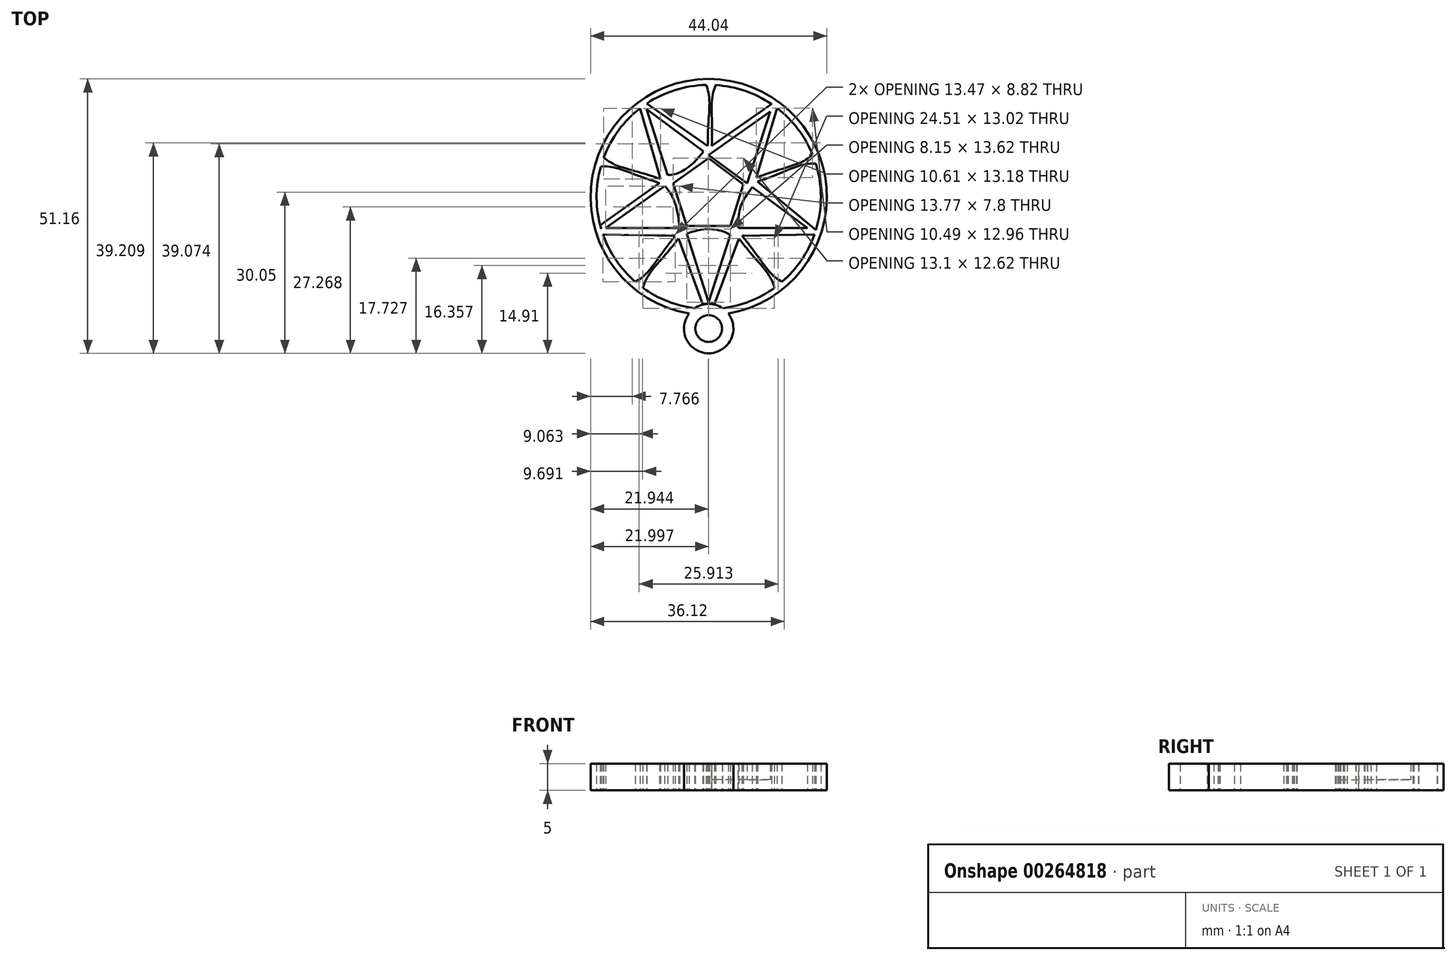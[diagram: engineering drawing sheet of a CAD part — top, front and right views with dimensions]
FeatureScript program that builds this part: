
annotation { "Feature Type Name" : "Feature", "Feature Type Description" : "" }
export const myFeature = defineFeature(function(context is Context, id is Id, definition is map)
    precondition{}
    {
        {
            var Q0;
            Q0=qCreatedBy(makeId("Top.planeOp"),FACE);
            var sketch = newSketch(context, id + "F0", { "sketchPlane" : qUnion([Q0])});
            skCircle(sketch, "E0", {"center": v(0, 0) * mm, "radius": 22.02 * mm});
            skLineSegment(sketch, "E1", {"start": v(0, 0) * mm, "end": v(0, 22.02) * mm, "construction": true});
            skLineSegment(sketch, "E2", {"start": v(0, 0) * mm, "end": v(20.72, 7.45) * mm, "construction": true});
            skLineSegment(sketch, "E3", {"start": v(0, 0) * mm, "end": v(13.06, -17.72) * mm, "construction": true});
            skLineSegment(sketch, "E4", {"start": v(0, 0) * mm, "end": v(-13.06, -17.72) * mm, "construction": true});
            skLineSegment(sketch, "E5", {"start": v(0, 0) * mm, "end": v(-20.91, 6.88) * mm, "construction": true});
            skLineSegment(sketch, "E6", {"start": v(-13.06, 17.72) * mm, "end": v(0, -22.02) * mm, "construction": true});
            skLineSegment(sketch, "E7", {"start": v(0, -22.02) * mm, "end": v(13.06, 17.72) * mm, "construction": true});
            skLineSegment(sketch, "E8", {"start": v(13.06, 17.72) * mm, "end": v(-20.91, -6.88) * mm, "construction": true});
            skLineSegment(sketch, "E9", {"start": v(-20.91, -6.88) * mm, "end": v(20.72, -6.88) * mm, "construction": true});
            skLineSegment(sketch, "E10", {"start": v(20.72, -6.88) * mm, "end": v(-13.06, 17.72) * mm, "construction": true});
            skCircle(sketch, "E11", {"center": v(0, 0) * mm, "radius": 20.9 * mm});
            skLineSegment(sketch, "E12", {"start": v(-11.47, 15.95) * mm, "end": v(0, -18.94) * mm});
            skLineSegment(sketch, "E13", {"start": v(0, -18.94) * mm, "end": v(11.36, 15.61) * mm});
            skLineSegment(sketch, "E14", {"start": v(11.36, 15.61) * mm, "end": v(-18.96, -5.83) * mm});
            skLineSegment(sketch, "E15", {"start": v(-18.96, -5.83) * mm, "end": v(18.12, -5.83) * mm});
            skLineSegment(sketch, "E16", {"start": v(18.12, -5.83) * mm, "end": v(-11.47, 15.95) * mm});
            skSolve(sketch);
        }
        {
            var Q0;
            Q0=makeQuery(id+"F0.imprint","IMPRINT",FACE,{"disambiguationData":[TD([[makeQuery(id+"F0.imprint","IMPRINT",EDGE,{"derivedFrom":sQuery(id+"F0.wireOp",EDGE,"E11")}),1.0]])]});
            var Q1;
            {var subQ0=sQuery(id+"F0.wireOp",EDGE,"E14");var subQ1=sQuery(id+"F0.wireOp",EDGE,"E13");var subQ2=makeQuery(id+"F0.imprint","INTERSECT",VERTEX,{"derivedFrom":[subQ1,subQ0]});Q1=makeQuery(id+"F0.imprint","IMPRINT",FACE,{"disambiguationData":[TD([[makeQuery(id+"F0.imprint","IMPRINT",EDGE,{"disambiguationData":[TD([[subQ2,1.0]])],"derivedFrom":subQ1}),1.0]])]});}
            var Q2;
            {var subQ0=sQuery(id+"F0.wireOp",EDGE,"E16");var subQ1=sQuery(id+"F0.wireOp",EDGE,"E12");var subQ2=makeQuery(id+"F0.imprint","INTERSECT",VERTEX,{"derivedFrom":[subQ1,subQ0]});Q2=makeQuery(id+"F0.imprint","IMPRINT",FACE,{"disambiguationData":[TD([[makeQuery(id+"F0.imprint","IMPRINT",EDGE,{"disambiguationData":[TD([[subQ2,-1.0]])],"derivedFrom":subQ1}),1.0]])]});}
            var Q3;
            {var subQ0=sQuery(id+"F0.wireOp",EDGE,"E14");var subQ1=sQuery(id+"F0.wireOp",EDGE,"E12");var subQ2=makeQuery(id+"F0.imprint","INTERSECT",VERTEX,{"derivedFrom":[subQ1,subQ0]});Q3=makeQuery(id+"F0.imprint","IMPRINT",FACE,{"disambiguationData":[TD([[makeQuery(id+"F0.imprint","IMPRINT",EDGE,{"disambiguationData":[TD([[subQ2,-1.0]])],"derivedFrom":subQ1}),-1.0]])]});}
            var Q4;
            {var subQ0=sQuery(id+"F0.wireOp",EDGE,"E13");var subQ1=sQuery(id+"F0.wireOp",EDGE,"E12");var subQ2=makeQuery(id+"F0.imprint","INTERSECT",VERTEX,{"derivedFrom":[subQ1,subQ0]});Q4=makeQuery(id+"F0.imprint","IMPRINT",FACE,{"disambiguationData":[TD([[makeQuery(id+"F0.imprint","IMPRINT",EDGE,{"disambiguationData":[TD([[subQ2,1.0]])],"derivedFrom":subQ1}),1.0]])]});}
            var Q5;
            {var subQ0=sQuery(id+"F0.wireOp",EDGE,"E15");var subQ1=sQuery(id+"F0.wireOp",EDGE,"E13");var subQ2=makeQuery(id+"F0.imprint","INTERSECT",VERTEX,{"derivedFrom":[subQ1,subQ0]});Q5=makeQuery(id+"F0.imprint","IMPRINT",FACE,{"disambiguationData":[TD([[makeQuery(id+"F0.imprint","IMPRINT",EDGE,{"disambiguationData":[TD([[subQ2,-1.0]])],"derivedFrom":subQ1}),-1.0]])]});}
            var Q6;
            {var subQ1=sQuery(id+"F0.wireOp",EDGE,"E12");var subQ5=sQuery(id+"F0.wireOp",EDGE,"E14");var subQ6=makeQuery(id+"F0.imprint","INTERSECT",VERTEX,{"derivedFrom":[subQ1,subQ5]});Q6=makeQuery(id+"F0.imprint","IMPRINT",FACE,{"disambiguationData":[TD([[makeQuery(id+"F0.imprint","IMPRINT",EDGE,{"disambiguationData":[TD([[subQ6,-1.0]])],"derivedFrom":subQ1}),1.0]])]});}
            extrude(context, id + "F1", {"entities" : qUnion([Q0, Q1, Q2, Q3, Q4, Q5, Q6]), "depth" : 2 * mm, "offsetDistance" : 25 * mm});
        }
        {
            var Q0;
            Q0=makeQuery(id+"F0.imprint","IMPRINT",FACE,{"disambiguationData":[TD([[makeQuery(id+"F0.imprint","IMPRINT",EDGE,{"derivedFrom":sQuery(id+"F0.wireOp",EDGE,"E0")}),1.0]])]});
            extrude(context, id + "F2", {"entities" : qUnion([Q0]), "operationType" : NewBodyOperationType.ADD, "depth" : 5 * mm, "offsetDistance" : 25 * mm});
        }
        {
            var Q0;
            Q0=makeQuery(id+"F1.opExtrude","CAP_FACE",FACE,{"disambiguationData":[OSD([sQuery(id+"F0.wireOp",EDGE,"E11")])],"isStart":false});
            var sketch = newSketch(context, id + "F3", { "sketchPlane" : qUnion([Q0])});
            skLineSegment(sketch, "E17", {"start": v(-11.59, 16.36) * mm, "end": v(0, -19.6) * mm});
            skLineSegment(sketch, "E18", {"start": v(0, -19.6) * mm, "end": v(11.46, 15.95) * mm});
            skLineSegment(sketch, "E19", {"start": v(11.46, 15.95) * mm, "end": v(-19.22, -5.77) * mm});
            skLineSegment(sketch, "E20", {"start": v(-19.22, -5.77) * mm, "end": v(18.4, -5.77) * mm});
            skLineSegment(sketch, "E21", {"start": v(18.4, -5.77) * mm, "end": v(-11.59, 16.36) * mm});
            skPoint(sketch, "E22.2.internal.snap0", {"position": v(-3.88, 5.1) * mm});
            skFitSpline(sketch, "E22", {"points": [v(-7.63, 4.09) * mm, v(-6, 4.35) * mm, v(-3.88, 5.51) * mm, v(-1.86, 7.4) * mm, v(-0.97, 8.52) * mm], "startDerivative": vector(7.1, 0.61) * mm, "endDerivative": vector(3.7, 5) * mm});
            skFitSpline(sketch, "E23.MirrorCS", {"points": [v(7.63, 4.09) * mm, v(6, 4.35) * mm, v(3.88, 5.51) * mm, v(1.86, 7.4) * mm, v(0.97, 8.52) * mm], "startDerivative": vector(-7.1, 0.61) * mm, "endDerivative": vector(-3.7, 5) * mm});
            skFitSpline(sketch, "E24", {"points": [v(0.97, 8.52) * mm, v(1.86, 7.4) * mm, v(3.88, 5.51) * mm, v(6, 4.35) * mm, v(7.63, 4.09) * mm], "startDerivative": vector(3.71, -5.02) * mm, "endDerivative": vector(7.1, -0.61) * mm});
            skFitSpline(sketch, "E25", {"points": [v(-8.2, 2.03) * mm, v(-7.19, 0.78) * mm, v(-6.13, -1.62) * mm, v(-5.57, -4.53) * mm, v(-5.44, -5.77) * mm], "startDerivative": vector(4.84, -5) * mm, "endDerivative": vector(0.3, -5.7) * mm});
            skPoint(sketch, "E26", {"position": v(-5.8, -1.62) * mm});
            skFitSpline(sketch, "E27", {"points": [v(-4.1, -6.89) * mm, v(-2.2, -6.27) * mm, v(0, -5.98) * mm, v(2.75, -6.44) * mm, v(4.05, -7.03) * mm], "startDerivative": vector(7.54, 3.7) * mm, "endDerivative": vector(5.89, -2.67) * mm});
            skFitSpline(sketch, "E28", {"points": [v(8.1, 1.83) * mm, v(6.5, -0.54) * mm, v(5.83, -2.25) * mm, v(5.5, -4.78) * mm, v(5.54, -5.77) * mm], "startDerivative": vector(-5.96, -8.34) * mm, "endDerivative": vector(0.52, -4.8) * mm});
            skFitSpline(sketch, "E29", {"points": [v(-20.36, 5.66) * mm, v(-17.82, 5.55) * mm, v(-12.86, 3.85) * mm, v(-9.19, 2.62) * mm], "startDerivative": vector(8.48, 0.55) * mm, "endDerivative": vector(10.23, -3.2) * mm});
            skFitSpline(sketch, "E30.MirrorCS", {"points": [v(-19.75, 7.53) * mm, v(-17.64, 6.1) * mm, v(-12.63, 4.53) * mm, v(-8.95, 3.34) * mm], "startDerivative": vector(6.5, -5.47) * mm, "endDerivative": vector(10.13, -3.49) * mm});
            skLineSegment(sketch, "E31", {"start": v(-19.22, -5.77) * mm, "end": v(0, 0) * mm, "construction": true});
            skLineSegment(sketch, "E32", {"start": v(0, 0) * mm, "end": v(11.46, 15.95) * mm, "construction": true});
            skLineSegment(sketch, "E33", {"start": v(-11.59, 16.36) * mm, "end": v(-10.84, 15.8) * mm, "construction": true});
            skLineSegment(sketch, "E34", {"start": v(-11.59, 16.36) * mm, "end": v(0, 0) * mm, "construction": true});
            skLineSegment(sketch, "E35", {"start": v(0, -0.7) * mm, "end": v(0, 0) * mm, "construction": true});
            skFitSpline(sketch, "E36.MirrorCS", {"points": [v(-13.87, -15.94) * mm, v(-11.8, -14.46) * mm, v(-8.6, -10.3) * mm, v(-6.22, -7.25) * mm], "startDerivative": vector(7.38, 4.21) * mm, "endDerivative": vector(6.77, 8.3) * mm});
            skFitSpline(sketch, "E37.MirrorCS", {"points": [v(-12.33, -17.17) * mm, v(-11.35, -14.82) * mm, v(-8.05, -10.74) * mm, v(-5.62, -7.72) * mm], "startDerivative": vector(2.4, 8.15) * mm, "endDerivative": vector(6.53, 8.5) * mm});
            skFitSpline(sketch, "E38.MirrorCS", {"points": [v(1.41, 21.09) * mm, v(0.67, 18.65) * mm, v(0.63, 13.4) * mm, v(0.57, 9.54) * mm], "startDerivative": vector(-3.33, -7.82) * mm, "endDerivative": vector(-0.37, -10.7) * mm});
            skFitSpline(sketch, "E39.MirrorCS", {"points": [v(-0.56, 21.13) * mm, v(0.09, 18.67) * mm, v(-0.08, 13.42) * mm, v(-0.19, 9.55) * mm], "startDerivative": vector(3, -7.94) * mm, "endDerivative": vector(-0.07, -10.72) * mm});
            skFitSpline(sketch, "E40.MirrorCS", {"points": [v(19.53, 8.08) * mm, v(17.46, 6.6) * mm, v(12.5, 4.88) * mm, v(8.85, 3.59) * mm], "startDerivative": vector(-6.34, -5.65) * mm, "endDerivative": vector(-10.03, -3.77) * mm});
            skFitSpline(sketch, "E41.MirrorCS", {"points": [v(20.2, 6.22) * mm, v(17.66, 6.05) * mm, v(12.74, 4.2) * mm, v(9.1, 2.87) * mm], "startDerivative": vector(-8.49, 0.31) * mm, "endDerivative": vector(-10.13, -3.49) * mm});
            skFitSpline(sketch, "E42.MirrorCS", {"points": [v(12.33, -17.17) * mm, v(11.35, -14.82) * mm, v(8.05, -10.74) * mm, v(5.62, -7.72) * mm], "startDerivative": vector(-2.4, 8.15) * mm, "endDerivative": vector(-6.53, 8.5) * mm});
            skFitSpline(sketch, "E43.MirrorCS", {"points": [v(13.87, -15.94) * mm, v(11.8, -14.46) * mm, v(8.6, -10.3) * mm, v(6.22, -7.25) * mm], "startDerivative": vector(-7.38, 4.21) * mm, "endDerivative": vector(-6.77, 8.3) * mm});
            skLineSegment(sketch, "E44", {"start": v(0, 0) * mm, "end": v(18.4, -5.77) * mm, "construction": true});
            skLineSegment(sketch, "E45", {"start": v(-19.76, -7) * mm, "end": v(-6.22, -7.25) * mm});
            skLineSegment(sketch, "E46", {"start": v(-19.76, -7) * mm, "end": v(-20.22, -5.27) * mm});
            skLineSegment(sketch, "E47", {"start": v(-20.22, -5.27) * mm, "end": v(-9.19, 2.62) * mm});
            skLineSegment(sketch, "E48", {"start": v(-19.75, 7.53) * mm, "end": v(-20.36, 5.66) * mm});
            skLineSegment(sketch, "E49", {"start": v(-13.87, -15.94) * mm, "end": v(-12.33, -17.17) * mm});
            skLineSegment(sketch, "E50", {"start": v(-5.62, -7.72) * mm, "end": v(-0.76, -20.96) * mm});
            skLineSegment(sketch, "E51", {"start": v(-0.76, -20.96) * mm, "end": v(0.71, -20.99) * mm});
            skLineSegment(sketch, "E52", {"start": v(0.71, -20.99) * mm, "end": v(5.62, -7.72) * mm});
            skLineSegment(sketch, "E53", {"start": v(12.33, -17.17) * mm, "end": v(13.87, -15.94) * mm});
            skLineSegment(sketch, "E54", {"start": v(6.22, -7.25) * mm, "end": v(19.85, -7) * mm});
            skLineSegment(sketch, "E55", {"start": v(19.85, -7) * mm, "end": v(20.08, -6.26) * mm});
            skLineSegment(sketch, "E56", {"start": v(9.1, 2.87) * mm, "end": v(20.08, -6.26) * mm});
            skLineSegment(sketch, "E57", {"start": v(19.53, 8.08) * mm, "end": v(20.2, 6.22) * mm});
            skLineSegment(sketch, "E58", {"start": v(8.85, 3.59) * mm, "end": v(12.8, 16.66) * mm});
            skLineSegment(sketch, "E59", {"start": v(12.8, 16.66) * mm, "end": v(11.8, 17.4) * mm});
            skLineSegment(sketch, "E60", {"start": v(11.8, 17.4) * mm, "end": v(0.57, 9.54) * mm});
            skLineSegment(sketch, "E61", {"start": v(1.41, 21.09) * mm, "end": v(-0.56, 21.13) * mm});
            skLineSegment(sketch, "E62", {"start": v(-0.19, 9.55) * mm, "end": v(-11.66, 17.51) * mm});
            skLineSegment(sketch, "E63", {"start": v(-11.66, 17.51) * mm, "end": v(-12.84, 16.68) * mm});
            skLineSegment(sketch, "E64", {"start": v(-12.84, 16.68) * mm, "end": v(-8.95, 3.34) * mm});
            skLineSegment(sketch, "E65", {"start": v(-6.63, 2.52) * mm, "end": v(-4.07, -5.4) * mm});
            skLineSegment(sketch, "E66", {"start": v(-4.07, -5.4) * mm, "end": v(4.07, -5.4) * mm});
            skLineSegment(sketch, "E67", {"start": v(4.07, -5.4) * mm, "end": v(6.47, 2.38) * mm});
            skLineSegment(sketch, "E68", {"start": v(6.47, 2.38) * mm, "end": v(0, 7.22) * mm});
            skLineSegment(sketch, "E69", {"start": v(0, 7.22) * mm, "end": v(-6.63, 2.52) * mm});
            skCircle(sketch, "E70", {"center": v(0, -24.64) * mm, "radius": 4.75 * mm});
            skCircle(sketch, "E71", {"center": v(0, -24.64) * mm, "radius": 2.5 * mm});
            skLineSegment(sketch, "E72", {"start": v(2.5, -24.53) * mm, "end": v(-2.5, -24.64) * mm, "construction": true});
            skSolve(sketch);
        }
        {
            var Q0;
            {var subQ3=sQuery(id+"F3.wireOp",EDGE,"E22");Q0=makeQuery(id+"F3.imprint","IMPRINT",FACE,{"disambiguationData":[TD([[makeQuery(id+"F3.imprint","IMPRINT",EDGE,{"derivedFrom":subQ3}),1.0]])]});}
            var Q1;
            {var subQ3=sQuery(id+"F3.wireOp",EDGE,"E24");var subQ6=makeQuery(id+"F3.imprint","IMPRINT",VERTEX,{"derivedFrom":subQ3});Q1=makeQuery(id+"F3.imprint","IMPRINT",FACE,{"disambiguationData":[TD([[makeQuery(id+"F3.imprint","IMPRINT",EDGE,{"disambiguationData":[TD([[subQ6,1.0]])],"derivedFrom":subQ3}),1.0]])]});}
            var Q2;
            {var subQ3=sQuery(id+"F3.wireOp",EDGE,"E25");Q2=makeQuery(id+"F3.imprint","IMPRINT",FACE,{"disambiguationData":[TD([[makeQuery(id+"F3.imprint","IMPRINT",EDGE,{"derivedFrom":subQ3}),-1.0]])]});}
            var Q3;
            {var subQ3=sQuery(id+"F3.wireOp",EDGE,"E27");Q3=makeQuery(id+"F3.imprint","IMPRINT",FACE,{"disambiguationData":[TD([[makeQuery(id+"F3.imprint","IMPRINT",EDGE,{"derivedFrom":subQ3}),-1.0]])]});}
            var Q4;
            {var subQ3=sQuery(id+"F3.wireOp",EDGE,"E28");Q4=makeQuery(id+"F3.imprint","IMPRINT",FACE,{"disambiguationData":[TD([[makeQuery(id+"F3.imprint","IMPRINT",EDGE,{"derivedFrom":subQ3}),1.0]])]});}
            var Q5;
            Q5=makeQuery(id+"F3.imprint","IMPRINT",FACE,{"disambiguationData":[TD([[makeQuery(id+"F3.imprint","IMPRINT",EDGE,{"derivedFrom":sQuery(id+"F3.wireOp",EDGE,"E65")}),1.0]])]});
            extrude(context, id + "F4", {"entities" : qUnion([Q0, Q1, Q2, Q3, Q4, Q5]), "operationType" : NewBodyOperationType.ADD, "depth" : 2 * mm, "offsetDistance" : 25 * mm});
        }
        {
            var Q0;
            Q0=makeQuery(id+"F3.imprint","IMPRINT",FACE,{"disambiguationData":[TD([[makeQuery(id+"F3.imprint","IMPRINT",EDGE,{"derivedFrom":sQuery(id+"F3.wireOp",EDGE,"E29")}),1.0]])]});
            var Q1;
            {var subQ5=sQuery(id+"F3.wireOp",EDGE,"E25");Q1=makeQuery(id+"F3.imprint","IMPRINT",FACE,{"disambiguationData":[TD([[makeQuery(id+"F3.imprint","IMPRINT",EDGE,{"derivedFrom":subQ5}),1.0]])]});}
            var Q2;
            {var subQ0=sQuery(id+"F3.wireOp",EDGE,"E22");Q2=makeQuery(id+"F3.imprint","IMPRINT",FACE,{"disambiguationData":[TD([[makeQuery(id+"F3.imprint","IMPRINT",EDGE,{"derivedFrom":subQ0}),-1.0]])]});}
            var Q3;
            {var subQ5=sQuery(id+"F3.wireOp",EDGE,"E24");var subQ7=makeQuery(id+"F3.imprint","IMPRINT",VERTEX,{"derivedFrom":subQ5});Q3=makeQuery(id+"F3.imprint","IMPRINT",FACE,{"disambiguationData":[TD([[makeQuery(id+"F3.imprint","IMPRINT",EDGE,{"disambiguationData":[TD([[subQ7,1.0]])],"derivedFrom":subQ5}),-1.0]])]});}
            var Q4;
            {var subQ5=sQuery(id+"F3.wireOp",EDGE,"E28");Q4=makeQuery(id+"F3.imprint","IMPRINT",FACE,{"disambiguationData":[TD([[makeQuery(id+"F3.imprint","IMPRINT",EDGE,{"derivedFrom":subQ5}),-1.0]])]});}
            var Q5;
            Q5=makeQuery(id+"F3.imprint","IMPRINT",FACE,{"disambiguationData":[TD([[makeQuery(id+"F3.imprint","IMPRINT",EDGE,{"derivedFrom":sQuery(id+"F3.wireOp",EDGE,"E65")}),-1.0]])]});
            var Q6;
            {var subQ0=sQuery(id+"F3.wireOp",EDGE,"E27");Q6=makeQuery(id+"F3.imprint","IMPRINT",FACE,{"disambiguationData":[TD([[makeQuery(id+"F3.imprint","IMPRINT",EDGE,{"derivedFrom":subQ0}),1.0]])]});}
            var Q7;
            {var subQ33=sQuery(id+"F3.wireOp",EDGE,"E47");Q7=makeQuery(id+"F3.imprint","IMPRINT",FACE,{"disambiguationData":[TD([[makeQuery(id+"F3.imprint","IMPRINT",EDGE,{"derivedFrom":subQ33}),-1.0]])]});}
            extrude(context, id + "F5", {"entities" : qUnion([Q0, Q1, Q2, Q3, Q4, Q5, Q6, Q7]), "operationType" : NewBodyOperationType.ADD, "depth" : 3 * mm, "offsetDistance" : 25 * mm});
        }
        {
            var Q0;
            Q0=qCreatedBy(makeId("Top.planeOp"),FACE);
            var sketch = newSketch(context, id + "F6", { "sketchPlane" : qUnion([Q0])});
            skCircle(sketch, "E73", {"center": v(0, -24.54) * mm, "radius": 4.6 * mm});
            skCircle(sketch, "E74", {"center": v(0, -24.54) * mm, "radius": 2.49 * mm});
            skSolve(sketch);
        }
        {
            var Q0;
            Q0=makeQuery(id+"F6.imprint","IMPRINT",FACE,{"disambiguationData":[TD([[makeQuery(id+"F6.imprint","IMPRINT",EDGE,{"derivedFrom":sQuery(id+"F6.wireOp",EDGE,"E73")}),1.0]])]});
            extrude(context, id + "F7", {"entities" : qUnion([Q0]), "operationType" : NewBodyOperationType.ADD, "depth" : 5 * mm, "offsetDistance" : 25 * mm});
        }
        {
            var Q0;
            {var subQ0=sQuery(id+"F0.wireOp",EDGE,"E11");Q0=makeQuery(id+"F5.boolean.opBoolean","SPLIT",FACE,{"disambiguationData":[TD([makeQuery(id+"F5.opExtrude","SWEPT_FACE",FACE,{"disambiguationData":[OSD([sQuery(id+"F3.wireOp",EDGE,"E39.MirrorCS")])]})])],"derivedFrom":makeQuery(id+"F1.opExtrude","CAP_FACE",FACE,{"disambiguationData":[OSD([subQ0])],"isStart":false})});}
            var Q1;
            Q1=makeQuery(id+"F4.opExtrude","CAP_FACE",FACE,{"disambiguationData":[OSD([sQuery(id+"F3.wireOp",EDGE,"E17"),sQuery(id+"F3.wireOp",EDGE,"E21"),sQuery(id+"F3.wireOp",EDGE,"E22")])],"isStart":false});
            var Q2;
            {var subQ0=sQuery(id+"F0.wireOp",EDGE,"E11");Q2=makeQuery(id+"F5.boolean.opBoolean","SPLIT",FACE,{"disambiguationData":[TD([makeQuery(id+"F5.opExtrude","SWEPT_FACE",FACE,{"disambiguationData":[OSD([sQuery(id+"F3.wireOp",EDGE,"E30.MirrorCS")])]})])],"derivedFrom":makeQuery(id+"F1.opExtrude","CAP_FACE",FACE,{"disambiguationData":[OSD([subQ0])],"isStart":false})});}
            var Q3;
            {var subQ0=sQuery(id+"F0.wireOp",EDGE,"E11");Q3=makeQuery(id+"F5.boolean.opBoolean","SPLIT",FACE,{"disambiguationData":[TD([makeQuery(id+"F5.opExtrude","SWEPT_FACE",FACE,{"disambiguationData":[OSD([sQuery(id+"F3.wireOp",EDGE,"E29")])]})])],"derivedFrom":makeQuery(id+"F1.opExtrude","CAP_FACE",FACE,{"disambiguationData":[OSD([subQ0])],"isStart":false})});}
            var Q4;
            Q4=makeQuery(id+"F4.opExtrude","CAP_FACE",FACE,{"disambiguationData":[OSD([sQuery(id+"F3.wireOp",EDGE,"E19"),sQuery(id+"F3.wireOp",EDGE,"E20"),sQuery(id+"F3.wireOp",EDGE,"E25")])],"isStart":false});
            var Q5;
            {var subQ0=sQuery(id+"F0.wireOp",EDGE,"E11");Q5=makeQuery(id+"F5.boolean.opBoolean","SPLIT",FACE,{"disambiguationData":[TD([makeQuery(id+"F5.opExtrude","SWEPT_FACE",FACE,{"disambiguationData":[OSD([sQuery(id+"F3.wireOp",EDGE,"E36.MirrorCS")])]})])],"derivedFrom":makeQuery(id+"F1.opExtrude","CAP_FACE",FACE,{"disambiguationData":[OSD([subQ0])],"isStart":false})});}
            var Q6;
            {var subQ0=sQuery(id+"F0.wireOp",EDGE,"E11");Q6=makeQuery(id+"F5.boolean.opBoolean","SPLIT",FACE,{"disambiguationData":[TD([makeQuery(id+"F5.opExtrude","SWEPT_FACE",FACE,{"disambiguationData":[OSD([sQuery(id+"F3.wireOp",EDGE,"E37.MirrorCS")])]})])],"derivedFrom":makeQuery(id+"F1.opExtrude","CAP_FACE",FACE,{"disambiguationData":[OSD([subQ0])],"isStart":false})});}
            var Q7;
            Q7=makeQuery(id+"F4.opExtrude","CAP_FACE",FACE,{"disambiguationData":[OSD([sQuery(id+"F3.wireOp",EDGE,"E17"),sQuery(id+"F3.wireOp",EDGE,"E18"),sQuery(id+"F3.wireOp",EDGE,"E27")])],"isStart":false});
            var Q8;
            Q8=makeQuery(id+"F4.opExtrude","CAP_FACE",FACE,{"disambiguationData":[OSD([sQuery(id+"F3.wireOp",EDGE,"E65"),sQuery(id+"F3.wireOp",EDGE,"E66"),sQuery(id+"F3.wireOp",EDGE,"E67"),sQuery(id+"F3.wireOp",EDGE,"E68"),sQuery(id+"F3.wireOp",EDGE,"E69")])],"isStart":false});
            var Q9;
            {var subQ0=sQuery(id+"F0.wireOp",EDGE,"E11");Q9=makeQuery(id+"F5.boolean.opBoolean","SPLIT",FACE,{"disambiguationData":[TD([makeQuery(id+"F5.opExtrude","SWEPT_FACE",FACE,{"disambiguationData":[OSD([sQuery(id+"F3.wireOp",EDGE,"E43.MirrorCS")])]})])],"derivedFrom":makeQuery(id+"F1.opExtrude","CAP_FACE",FACE,{"disambiguationData":[OSD([subQ0])],"isStart":false})});}
            var Q10;
            Q10=makeQuery(id+"F4.opExtrude","CAP_FACE",FACE,{"disambiguationData":[OSD([sQuery(id+"F3.wireOp",EDGE,"E20"),sQuery(id+"F3.wireOp",EDGE,"E21"),sQuery(id+"F3.wireOp",EDGE,"E28")])],"isStart":false});
            var Q11;
            {var subQ0=sQuery(id+"F0.wireOp",EDGE,"E11");Q11=makeQuery(id+"F5.boolean.opBoolean","SPLIT",FACE,{"disambiguationData":[TD([makeQuery(id+"F5.opExtrude","SWEPT_FACE",FACE,{"disambiguationData":[OSD([sQuery(id+"F3.wireOp",EDGE,"E41.MirrorCS")])]})])],"derivedFrom":makeQuery(id+"F1.opExtrude","CAP_FACE",FACE,{"disambiguationData":[OSD([subQ0])],"isStart":false})});}
            var Q12;
            {var subQ0=sQuery(id+"F0.wireOp",EDGE,"E11");Q12=makeQuery(id+"F5.boolean.opBoolean","SPLIT",FACE,{"disambiguationData":[TD([makeQuery(id+"F5.opExtrude","SWEPT_FACE",FACE,{"disambiguationData":[OSD([sQuery(id+"F3.wireOp",EDGE,"E40.MirrorCS")])]})])],"derivedFrom":makeQuery(id+"F1.opExtrude","CAP_FACE",FACE,{"disambiguationData":[OSD([subQ0])],"isStart":false})});}
            var Q13;
            Q13=makeQuery(id+"F4.opExtrude","CAP_FACE",FACE,{"disambiguationData":[OSD([sQuery(id+"F3.wireOp",EDGE,"E18"),sQuery(id+"F3.wireOp",EDGE,"E19"),sQuery(id+"F3.wireOp",EDGE,"E24")])],"isStart":false});
            var Q14;
            {var subQ0=sQuery(id+"F0.wireOp",EDGE,"E11");Q14=makeQuery(id+"F5.boolean.opBoolean","SPLIT",FACE,{"disambiguationData":[TD([makeQuery(id+"F5.opExtrude","SWEPT_FACE",FACE,{"disambiguationData":[OSD([sQuery(id+"F3.wireOp",EDGE,"E38.MirrorCS")])]})])],"derivedFrom":makeQuery(id+"F1.opExtrude","CAP_FACE",FACE,{"disambiguationData":[OSD([subQ0])],"isStart":false})});}
            extrude(context, id + "F8", {"entities" : qUnion([Q0, Q1, Q2, Q3, Q4, Q5, Q6, Q7, Q8, Q9, Q10, Q11, Q12, Q13, Q14]), "operationType" : NewBodyOperationType.REMOVE, "oppositeDirection" : true, "depth" : 25 * mm, "offsetDistance" : 25 * mm});
        }
    });
